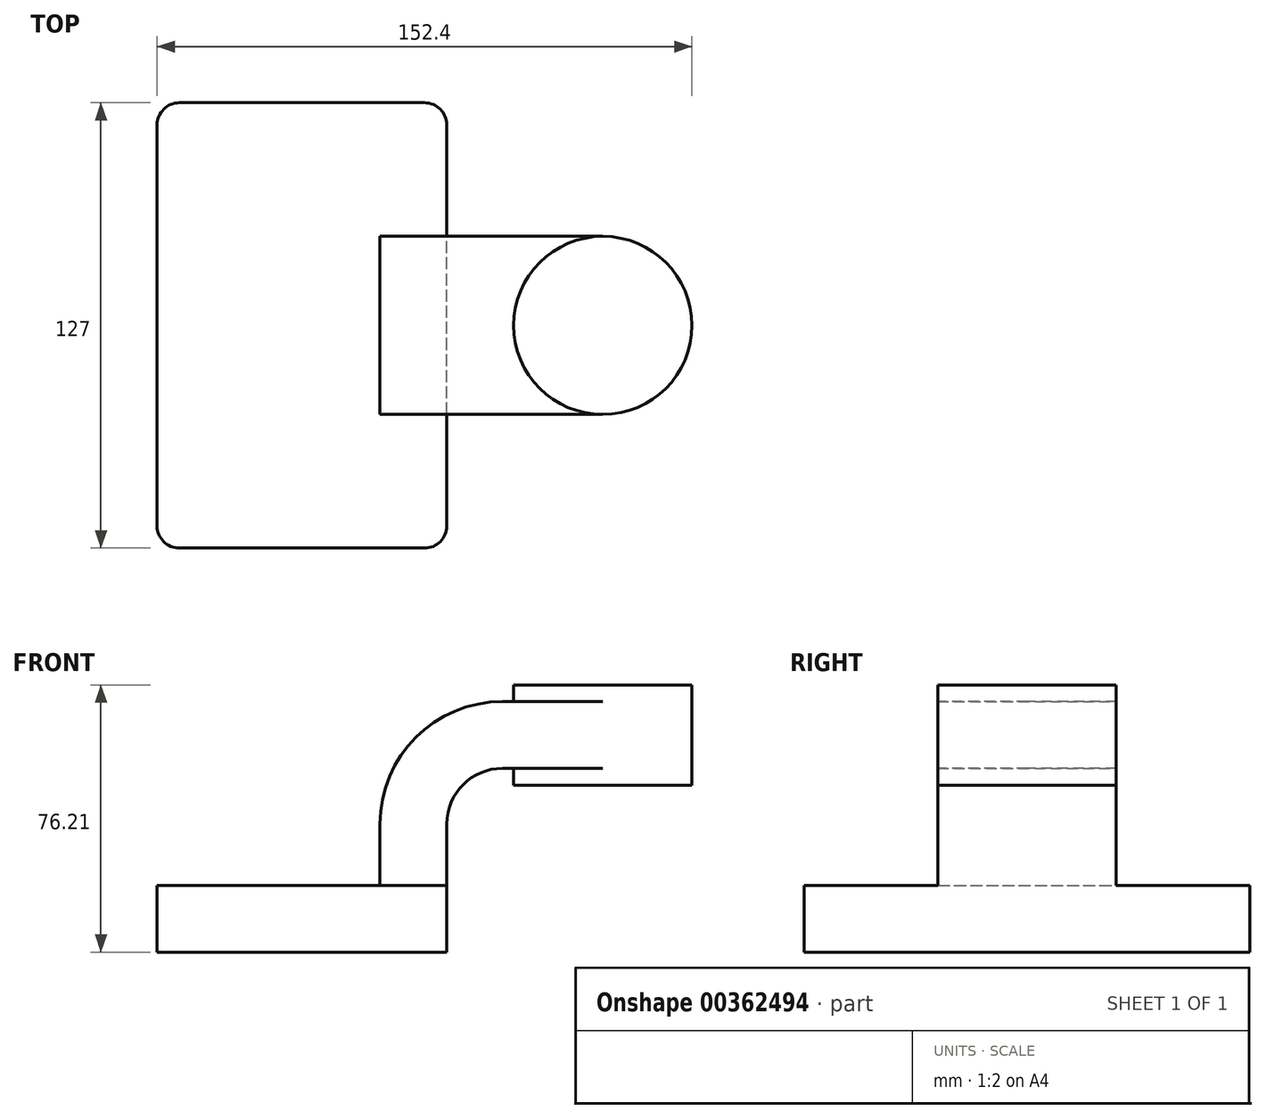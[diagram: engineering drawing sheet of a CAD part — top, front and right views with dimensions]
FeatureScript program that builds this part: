
annotation { "Feature Type Name" : "Feature", "Feature Type Description" : "" }
export const myFeature = defineFeature(function(context is Context, id is Id, definition is map)
    precondition{}
    {
        {
            var Q0;
            Q0=qCreatedBy(makeId("Front.planeOp"),FACE);
            var sketch = newSketch(context, id + "F0", { "sketchPlane" : qUnion([Q0])});
            skLineSegment(sketch, "E0.bottom", {"start": v(-41.28, 9.52) * mm, "end": v(41.27, 9.53) * mm});
            skLineSegment(sketch, "E0.top", {"start": v(-41.28, -9.53) * mm, "end": v(41.28, -9.53) * mm});
            skLineSegment(sketch, "E0.left", {"start": v(-41.28, 9.52) * mm, "end": v(-41.27, -9.53) * mm});
            skLineSegment(sketch, "E0.right", {"start": v(41.28, 9.53) * mm, "end": v(41.28, -9.52) * mm});
            skPoint(sketch, "E0.middle", {"position": v(0, 0) * mm});
            skLineSegment(sketch, "E1.bottom", {"start": v(60.32, 66.68) * mm, "end": v(111.12, 66.68) * mm});
            skLineSegment(sketch, "E1.top", {"start": v(60.32, 38.1) * mm, "end": v(111.12, 38.1) * mm});
            skLineSegment(sketch, "E1.left", {"start": v(60.32, 66.68) * mm, "end": v(60.32, 38.1) * mm});
            skLineSegment(sketch, "E1.right", {"start": v(111.12, 66.68) * mm, "end": v(111.12, 38.1) * mm});
            skPoint(sketch, "E1.middle", {"position": v(85.72, 52.39) * mm});
            skLineSegment(sketch, "E2", {"start": v(41.27, 9.53) * mm, "end": v(41.27, 27) * mm});
            skArc(sketch, "E3", {"start": v(41.27, 27) * mm, "mid": v(45.92, 38.23) * mm, "end": v(57.15, 42.88) * mm});
            skLineSegment(sketch, "E4", {"start": v(57.15, 42.88) * mm, "end": v(85.72, 42.88) * mm});
            skPoint(sketch, "E4.endSnap0", {"position": v(85.72, 38.1) * mm});
            skLineSegment(sketch, "E5.0", {"start": v(57.15, 61.93) * mm, "end": v(85.72, 61.93) * mm});
            skArc(sketch, "E5.1", {"start": v(22.22, 27) * mm, "mid": v(32.45, 51.7) * mm, "end": v(57.15, 61.93) * mm});
            skLineSegment(sketch, "E5.2", {"start": v(22.22, 9.53) * mm, "end": v(22.22, 27) * mm});
            skLineSegment(sketch, "E6", {"start": v(85.72, 38.1) * mm, "end": v(85.72, 66.68) * mm});
            skFitSpline(sketch, "E7", {"points": [v(-41.28, 9.53) * mm, v(57.15, 61.93) * mm], "startDerivative": vector(-0.57, 92.57) * mm, "endDerivative": vector(133.91, -0.33) * mm});
            skSolve(sketch);
        }
        {
            var Q0;
            Q0=makeQuery(id+"F0.imprint","IMPRINT",FACE,{"disambiguationData":[TD([[makeQuery(id+"F0.imprint","IMPRINT",EDGE,{"derivedFrom":sQuery(id+"F0.wireOp",EDGE,"E0.top")}),1.0]])]});
            extrude(context, id + "F1", {"entities" : qUnion([Q0]), "endBound" : BoundingType.SYMMETRIC, "depth" : 127 * mm});
        }
        {
            var Q0;
            {var subQ1=sQuery(id+"F0.wireOp",EDGE,"E2");Q0=makeQuery(id+"F0.imprint","IMPRINT",FACE,{"disambiguationData":[TD([[makeQuery(id+"F0.imprint","IMPRINT",EDGE,{"derivedFrom":subQ1}),1.0]])]});}
            var Q1;
            {var subQ0=sQuery(id+"F0.wireOp",EDGE,"E5.0");var subQ1=sQuery(id+"F0.wireOp",EDGE,"E1.left");var subQ2=makeQuery(id+"F0.imprint","INTERSECT",VERTEX,{"derivedFrom":[subQ1,subQ0]});Q1=makeQuery(id+"F0.imprint","IMPRINT",FACE,{"disambiguationData":[TD([[makeQuery(id+"F0.imprint","IMPRINT",EDGE,{"disambiguationData":[TD([[subQ2,-1.0]])],"derivedFrom":subQ1}),1.0]])]});}
            extrude(context, id + "F2", {"entities" : qUnion([Q0, Q1]), "operationType" : NewBodyOperationType.ADD, "endBound" : BoundingType.SYMMETRIC, "depth" : 50.8 * mm});
        }
        {
            var Q0;
            Q0=makeQuery(id+"F0.imprint","IMPRINT",FACE,{"disambiguationData":[TD([[makeQuery(id+"F0.imprint","IMPRINT",EDGE,{"derivedFrom":sQuery(id+"F0.wireOp",EDGE,"E5.1")}),1.0]])]});
            extrude(context, id + "F3", {"entities" : qUnion([Q0]), "operationType" : NewBodyOperationType.ADD, "endBound" : BoundingType.SYMMETRIC, "depth" : 15.88 * mm});
        }
        {
            var Q0;
            {var subQ0=sQuery(id+"F0.wireOp",EDGE,"E1.right");Q0=makeQuery(id+"F0.imprint","IMPRINT",FACE,{"disambiguationData":[TD([[makeQuery(id+"F0.imprint","IMPRINT",EDGE,{"derivedFrom":subQ0}),-1.0]])]});}
            var Q1;
            Q1=sQuery(id+"F0.wireOp",EDGE,"E6");
            revolve(context, id + "F4", {"operationType" : NewBodyOperationType.ADD, "entities" : qUnion([Q0]), "axis" : qUnion([Q1]), "revolveType" : RevolveType.FULL});
        }
        {
            var Q0;
            Q0=makeQuery(id+"F1.opExtrude","CAP_EDGE",EDGE,{"disambiguationData":[OSD([sQuery(id+"F0.wireOp",EDGE,"E0.right")])],"isStart":false});
            var Q1;
            Q1=makeQuery(id+"F1.opExtrude","CAP_EDGE",EDGE,{"disambiguationData":[OSD([sQuery(id+"F0.wireOp",EDGE,"E0.left")])],"isStart":false});
            var Q2;
            Q2=makeQuery(id+"F1.opExtrude","CAP_EDGE",EDGE,{"disambiguationData":[OSD([sQuery(id+"F0.wireOp",EDGE,"E0.right")])],"isStart":true});
            var Q3;
            Q3=makeQuery(id+"F1.opExtrude","CAP_EDGE",EDGE,{"disambiguationData":[OSD([sQuery(id+"F0.wireOp",EDGE,"E0.left")])],"isStart":true});
            fillet(context, id + "F5", {"entities" : qUnion([Q0, Q1, Q2, Q3]), "radius" : 6.35 * mm, "tangentPropagation" : true, "allowEdgeOverflow" : false});
        }
    });
